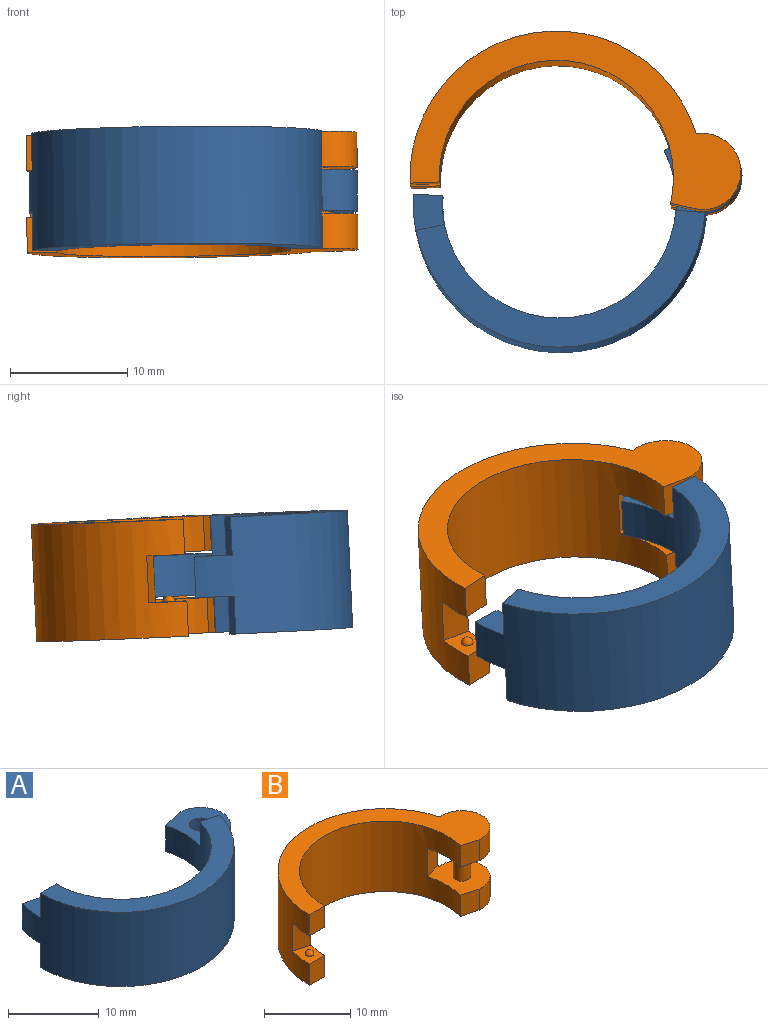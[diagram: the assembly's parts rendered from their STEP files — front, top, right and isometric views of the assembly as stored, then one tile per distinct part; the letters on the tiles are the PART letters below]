
ASSEMBLY  parts=2 mates=1
PART A: 17 faces, bbox 28.3x15.8x10 mm
  f0: plane 3.24x2.84mm, normal (0,0,1), area 7.4mm2, adj f2,f5,f6,f13
  f1: plane 3.24x2.84mm, normal (0,0,-1), area 6.6mm2, adj f2,f5,f6,f12,f16
  f2: cylinder r=12.5mm len=24.57mm, axis (0,0,-1), area 369.8mm2, adj f0,f1,f3,f6,f7,f8,f10,f11
  f3: cylinder r=3.26mm len=6.53mm, axis (0,0,-1), area 38.9mm2, adj f2,f4,f7,f8
  f4: plane 3.5x2.42mm, normal (-0.26,0.97,0), area 8.8mm2, adj f3,f5,f7,f8
  f5: cylinder r=10mm len=20mm, axis (0,0,-1), area 314.2mm2, adj f0,f1,f4,f6,f7,f8,f10,f11
  f6: plane 3.5x2.42mm, normal (0.26,0.97,0), area 8.8mm2, adj f0,f1,f2,f5
  f7: plane 6.74x6.16mm, normal (0,0,1), area 28mm2, adj f2,f3,f4,f5,f9,f14
  f8: plane 6.74x6.16mm, normal (0,0,-1), area 28mm2, adj f2,f3,f4,f5,f9,f11
  f9: cylinder r=1.25mm len=3.5mm, axis (0,0,1), area 27.5mm2, adj f7,f8
  f10: plane 24.51x12.5mm, normal (0,0,-1), area 80.4mm2, adj f2,f5,f11,f12
  f11: plane 3.25x2.4mm, normal (0.28,0.96,0), area 8.1mm2, adj f2,f5,f8,f10
  f12: plane 3.25x2.5mm, normal (0,1,0), area 8.1mm2, adj f1,f2,f5,f10
  f13: plane 3.25x2.5mm, normal (0,1,0), area 8.1mm2, adj f0,f2,f5,f15
  f14: plane 3.25x2.4mm, normal (0.28,0.96,0), area 8.1mm2, adj f2,f5,f7,f15
  f15: plane 24.51x12.5mm, normal (0,0,1), area 80.4mm2, adj f2,f5,f13,f14
  f16: sphere r=0.5mm, area 1.6mm2, adj f1
PART B: 18 faces, bbox 28.3x15.8x10 mm
  f0: plane 3.24x2.84mm, normal (0,0,1), area 6.6mm2, adj f3,f4,f5,f9,f17
  f1: plane 3x2.42mm, normal (-0.26,-0.97,0), area 7.5mm2, adj f2,f5,f6,f7
  f2: cylinder r=3.26mm len=6.53mm, axis (0,0,-1), area 33.3mm2, adj f1,f3,f6,f7
  f3: cylinder r=12.5mm len=24.57mm, axis (0,0,-1), area 345.9mm2, adj f0,f2,f4,f6,f7,f9,f10,f11
  f4: plane 3x2.5mm, normal (0,-1,0), area 7.5mm2, adj f0,f3,f5,f7
  f5: cylinder r=10mm len=20mm, axis (0,0,-1), area 308.1mm2, adj f0,f1,f4,f6,f7,f9,f10,f11
  f6: plane 6.74x6.16mm, normal (0,0,1), area 29.8mm2, adj f1,f2,f3,f5,f8,f10
  f7: plane 28.26x15.76mm, normal (0,0,-1), area 113.4mm2, adj f1,f2,f3,f4,f5
  f8: cylinder r=1mm len=4mm, axis (0,0,-1), area 25.1mm2, adj f6,f11
  f9: plane 4x2.42mm, normal (-0.26,-0.97,0), area 10mm2, adj f0,f3,f5,f12
  f10: plane 4x2.4mm, normal (0.28,-0.96,0), area 10mm2, adj f3,f5,f6,f11
  f11: plane 6.74x6.16mm, normal (0,0,-1), area 29.8mm2, adj f3,f5,f8,f10,f13,f14
  f12: plane 3.24x2.84mm, normal (0,0,-1), area 7.4mm2, adj f3,f5,f9,f15
  f13: plane 3x2.42mm, normal (-0.26,-0.97,0), area 7.5mm2, adj f5,f11,f14,f16
  f14: cylinder r=3.26mm len=6.53mm, axis (0,0,-1), area 33.3mm2, adj f3,f11,f13,f16
  f15: plane 3x2.5mm, normal (0,-1,0), area 7.5mm2, adj f3,f5,f12,f16
  f16: plane 28.26x15.76mm, normal (0,0,1), area 113.4mm2, adj f3,f5,f13,f14,f15
  f17: sphere r=0.5mm, area 1.6mm2, adj f0
PLACE A rot(axis=(-0.22,-0.03,0.97),11.9deg) t=(-7.22,10.06,-2.39)mm
PLACE B rot(axis=(-0.75,-0.15,0.64),3.5deg) t=(-7.43,11.93,-5.73)mm
MATE revolute B.f8 <-> A.f3  axis (0.01,-0.05,-1) through (5.01,12.65,-0.63)mm
